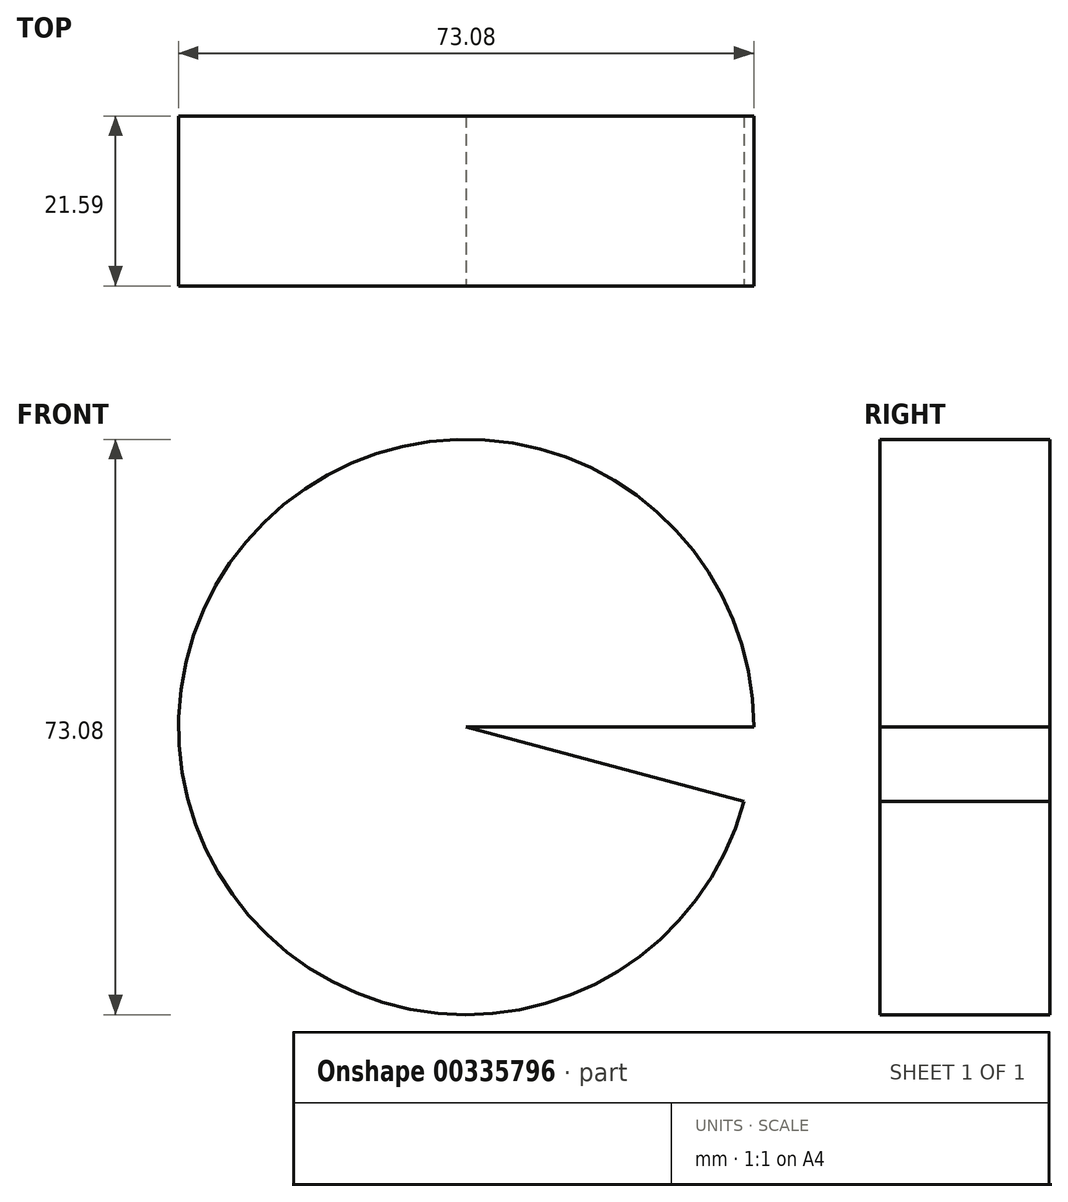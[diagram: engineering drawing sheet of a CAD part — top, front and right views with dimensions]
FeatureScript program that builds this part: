
annotation { "Feature Type Name" : "Feature", "Feature Type Description" : "" }
export const myFeature = defineFeature(function(context is Context, id is Id, definition is map)
    precondition{}
    {
        {
            var Q0;
            Q0=qCreatedBy(makeId("Top.planeOp"),FACE);
            var sketch = newSketch(context, id + "F0", { "sketchPlane" : qUnion([Q0])});
            skCircle(sketch, "E0", {"center": v(-62.28, 52.52) * mm, "radius": 11.18 * mm});
            skLineSegment(sketch, "E1.bottom", {"start": v(23.25, 37.16) * mm, "end": v(59.79, 37.16) * mm});
            skLineSegment(sketch, "E1.top", {"start": v(23.25, 15.57) * mm, "end": v(59.79, 15.57) * mm});
            skLineSegment(sketch, "E1.left", {"start": v(23.25, 37.16) * mm, "end": v(23.25, 15.57) * mm});
            skLineSegment(sketch, "E1.right", {"start": v(59.79, 37.16) * mm, "end": v(59.79, 15.57) * mm});
            skLineSegment(sketch, "E2", {"start": v(-55, -17.45) * mm, "end": v(-20.95, -29.08) * mm});
            skLineSegment(sketch, "E3", {"start": v(-20.95, -29.08) * mm, "end": v(-20.95, -63.13) * mm});
            skLineSegment(sketch, "E4", {"start": v(-20.95, -63.13) * mm, "end": v(-59.98, -69.35) * mm});
            skLineSegment(sketch, "E5", {"start": v(-59.98, -69.35) * mm, "end": v(-55, -17.45) * mm});
            skLineSegment(sketch, "E6", {"start": v(-44.62, -31.99) * mm, "end": v(-50.43, -55.24) * mm});
            skLineSegment(sketch, "E7", {"start": v(-50.43, -55.24) * mm, "end": v(-37.93, -58.36) * mm});
            skLineSegment(sketch, "E8", {"start": v(-37.93, -58.36) * mm, "end": v(-44.62, -31.99) * mm});
            skLineSegment(sketch, "E9", {"start": v(-82.91, 71.7) * mm, "end": v(-82.91, 30.26) * mm, "construction": true});
            skSolve(sketch);
        }
        {
            var Q0;
            Q0=makeQuery(id+"F0.imprint","IMPRINT",FACE,{"disambiguationData":[TD([[makeQuery(id+"F0.imprint","IMPRINT",EDGE,{"derivedFrom":sQuery(id+"F0.wireOp",EDGE,"E1.bottom")}),-1.0]])]});
            var Q1;
            Q1=sQuery(id+"F0.wireOp",EDGE,"E1.left");
            revolve(context, id + "F1", {"entities" : qUnion([Q0]), "axis" : qUnion([Q1]), "revolveType" : RevolveType.ONE_DIRECTION, "angle" : 345 * degree});
        }
    });
